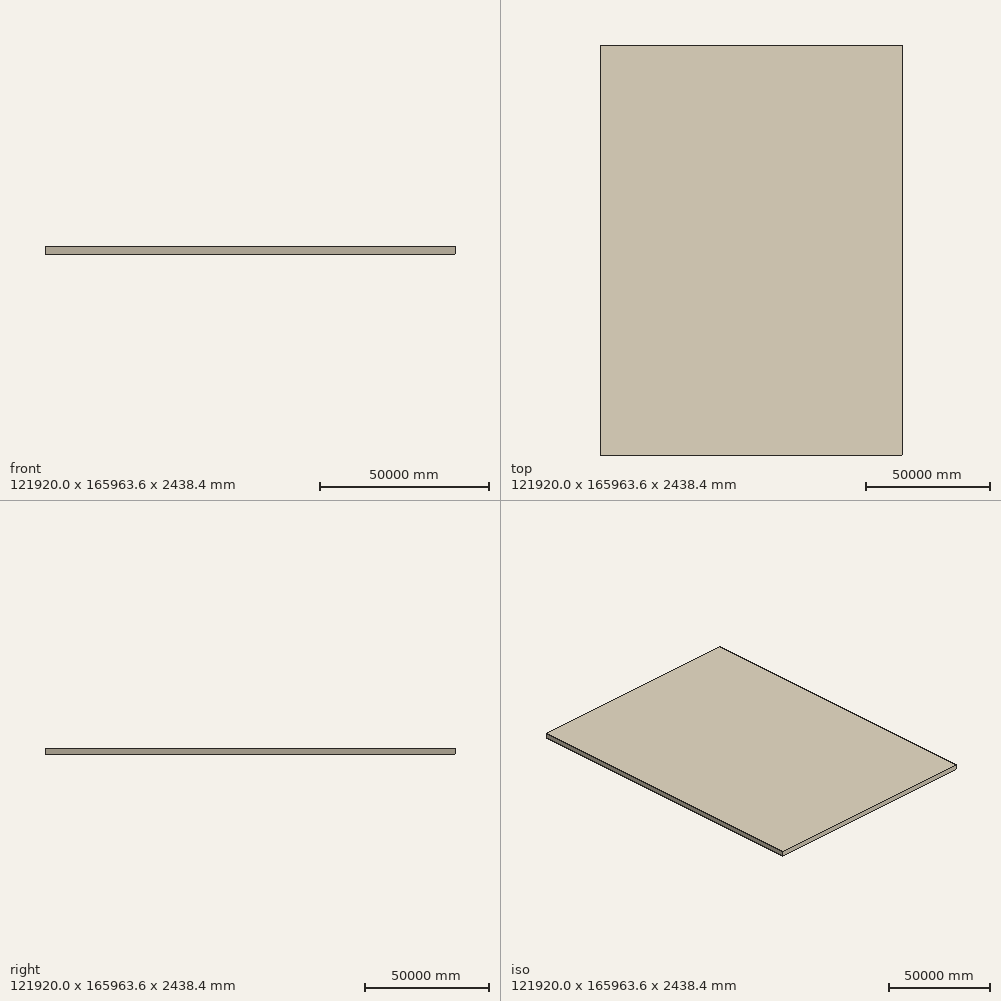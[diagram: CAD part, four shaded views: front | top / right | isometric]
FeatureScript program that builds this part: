
annotation { "Feature Type Name" : "Feature", "Feature Type Description" : "" }
export const myFeature = defineFeature(function(context is Context, id is Id, definition is map)
    precondition{}
    {
        {
            var Q0;
            Q0=qCreatedBy(makeId("Top.planeOp"),FACE);
            var sketch = newSketch(context, id + "F0", { "sketchPlane" : qUnion([Q0])});
            skLineSegment(sketch, "E0.bottom", {"start": v(0, 0) * mm, "end": v(121920, 0) * mm});
            skLineSegment(sketch, "E0.top", {"start": v(0, 165963.6) * mm, "end": v(121920, 165963.6) * mm});
            skLineSegment(sketch, "E0.left", {"start": v(0, 0) * mm, "end": v(0, 165963.6) * mm});
            skLineSegment(sketch, "E0.right", {"start": v(121920, 0) * mm, "end": v(121920, 165963.6) * mm});
            skSolve(sketch);
        }
        {
            var Q0;
            Q0 = qSketchRegion(id + "F0", true);
            extrude(context, id + "F1", {"entities" : qUnion([Q0]), "depth" : 2438.4 * mm, "offsetDistance" : 25.4 * mm});
        }
    });
